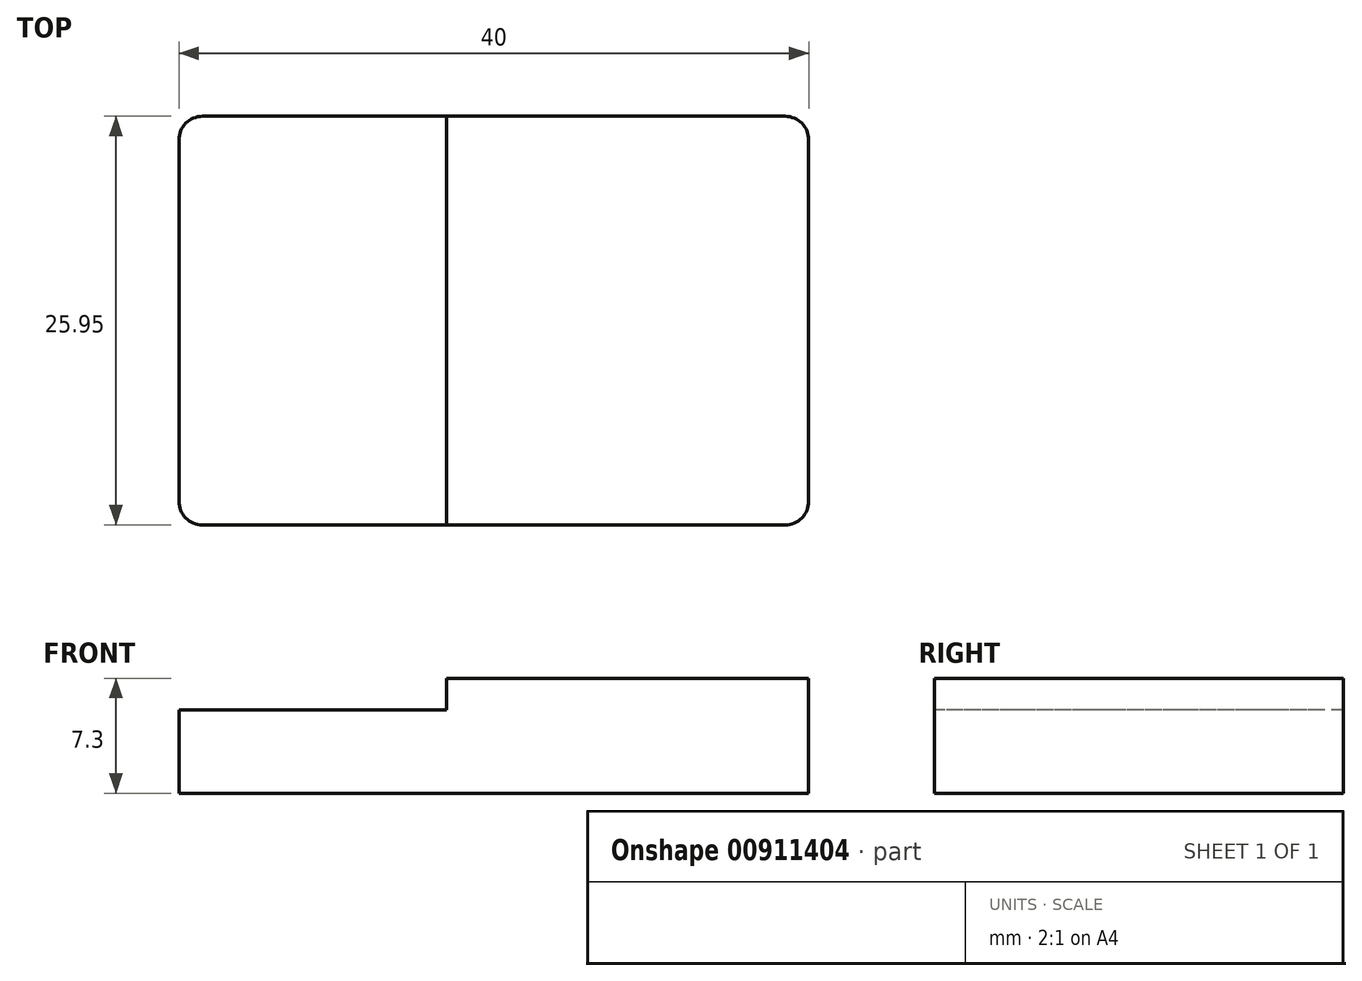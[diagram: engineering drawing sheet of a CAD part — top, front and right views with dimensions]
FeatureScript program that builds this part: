
annotation { "Feature Type Name" : "Feature", "Feature Type Description" : "" }
export const myFeature = defineFeature(function(context is Context, id is Id, definition is map)
    precondition{}
    {
        {
            var Q0;
            Q0=qCreatedBy(makeId("Top.planeOp"),FACE);
            var sketch = newSketch(context, id + "F0", { "sketchPlane" : qUnion([Q0])});
            skLineSegment(sketch, "E0.bottom", {"start": v(-60.17, 49.14) * mm, "end": v(-20.17, 49.14) * mm});
            skLineSegment(sketch, "E0.top", {"start": v(-60.17, 23.19) * mm, "end": v(-20.17, 23.19) * mm});
            skLineSegment(sketch, "E0.left", {"start": v(-60.17, 49.14) * mm, "end": v(-60.17, 23.19) * mm});
            skLineSegment(sketch, "E0.right", {"start": v(-20.17, 49.14) * mm, "end": v(-20.17, 23.19) * mm});
            skSolve(sketch);
        }
        {
            var Q0;
            Q0 = qSketchRegion(id + "F0", true);
            extrude(context, id + "F1", {"entities" : qUnion([Q0]), "depth" : 5.3 * mm, "offsetDistance" : 25 * mm});
        }
        {
            var Q0;
            Q0=makeQuery(id+"F1.opExtrude","CAP_FACE",FACE,{"disambiguationData":[OSD([sQuery(id+"F0.wireOp",EDGE,"E0.bottom"),sQuery(id+"F0.wireOp",EDGE,"E0.top"),sQuery(id+"F0.wireOp",EDGE,"E0.left"),sQuery(id+"F0.wireOp",EDGE,"E0.right")])],"isStart":false});
            var sketch = newSketch(context, id + "F2", { "sketchPlane" : qUnion([Q0])});
            skLineSegment(sketch, "E1.bottom", {"start": v(-43.17, 49.14) * mm, "end": v(-20.17, 49.14) * mm});
            skLineSegment(sketch, "E1.top", {"start": v(-43.17, 23.19) * mm, "end": v(-20.17, 23.19) * mm});
            skLineSegment(sketch, "E1.left", {"start": v(-43.17, 49.14) * mm, "end": v(-43.17, 23.19) * mm});
            skLineSegment(sketch, "E1.right", {"start": v(-20.17, 49.14) * mm, "end": v(-20.17, 23.19) * mm});
            skSolve(sketch);
        }
        {
            var Q0;
            Q0=makeQuery(id+"F2.imprint","IMPRINT",FACE,{"disambiguationData":[TD([[makeQuery(id+"F2.imprint","IMPRINT",EDGE,{"derivedFrom":sQuery(id+"F2.wireOp",EDGE,"E1.bottom")}),-1.0]])]});
            extrude(context, id + "F3", {"entities" : qUnion([Q0]), "operationType" : NewBodyOperationType.ADD, "depth" : 2 * mm, "offsetDistance" : 25 * mm});
        }
        {
            var Q0;
            Q0=makeQuery(id+"F3.boolean.opBoolean","MERGE",EDGE,{"derivedFrom":[makeQuery(id+"F1.opExtrude","SWEPT_EDGE",EDGE,{"disambiguationData":[OSD([sQuery(id+"F0.wireOp",EDGE,"E0.top"),sQuery(id+"F0.wireOp",EDGE,"E0.right")])]}),makeQuery(id+"F3.opExtrude","SWEPT_EDGE",EDGE,{"disambiguationData":[OSD([sQuery(id+"F2.wireOp",EDGE,"E1.top"),sQuery(id+"F2.wireOp",EDGE,"E1.right")])]})]});
            var Q1;
            Q1=makeQuery(id+"F3.boolean.opBoolean","MERGE",EDGE,{"derivedFrom":[makeQuery(id+"F1.opExtrude","SWEPT_EDGE",EDGE,{"disambiguationData":[OSD([sQuery(id+"F0.wireOp",EDGE,"E0.bottom"),sQuery(id+"F0.wireOp",EDGE,"E0.right")])]}),makeQuery(id+"F3.opExtrude","SWEPT_EDGE",EDGE,{"disambiguationData":[OSD([sQuery(id+"F2.wireOp",EDGE,"E1.bottom"),sQuery(id+"F2.wireOp",EDGE,"E1.right")])]})]});
            var Q2;
            Q2=makeQuery(id+"F1.opExtrude","SWEPT_EDGE",EDGE,{"disambiguationData":[OSD([sQuery(id+"F0.wireOp",EDGE,"E0.top"),sQuery(id+"F0.wireOp",EDGE,"E0.left")])]});
            var Q3;
            Q3=makeQuery(id+"F1.opExtrude","SWEPT_EDGE",EDGE,{"disambiguationData":[OSD([sQuery(id+"F0.wireOp",EDGE,"E0.bottom"),sQuery(id+"F0.wireOp",EDGE,"E0.left")])]});
            fillet(context, id + "F4", {"entities" : qUnion([Q0, Q1, Q2, Q3]), "radius" : 1.5 * mm, "tangentPropagation" : true, "allowEdgeOverflow" : false});
        }
    });
